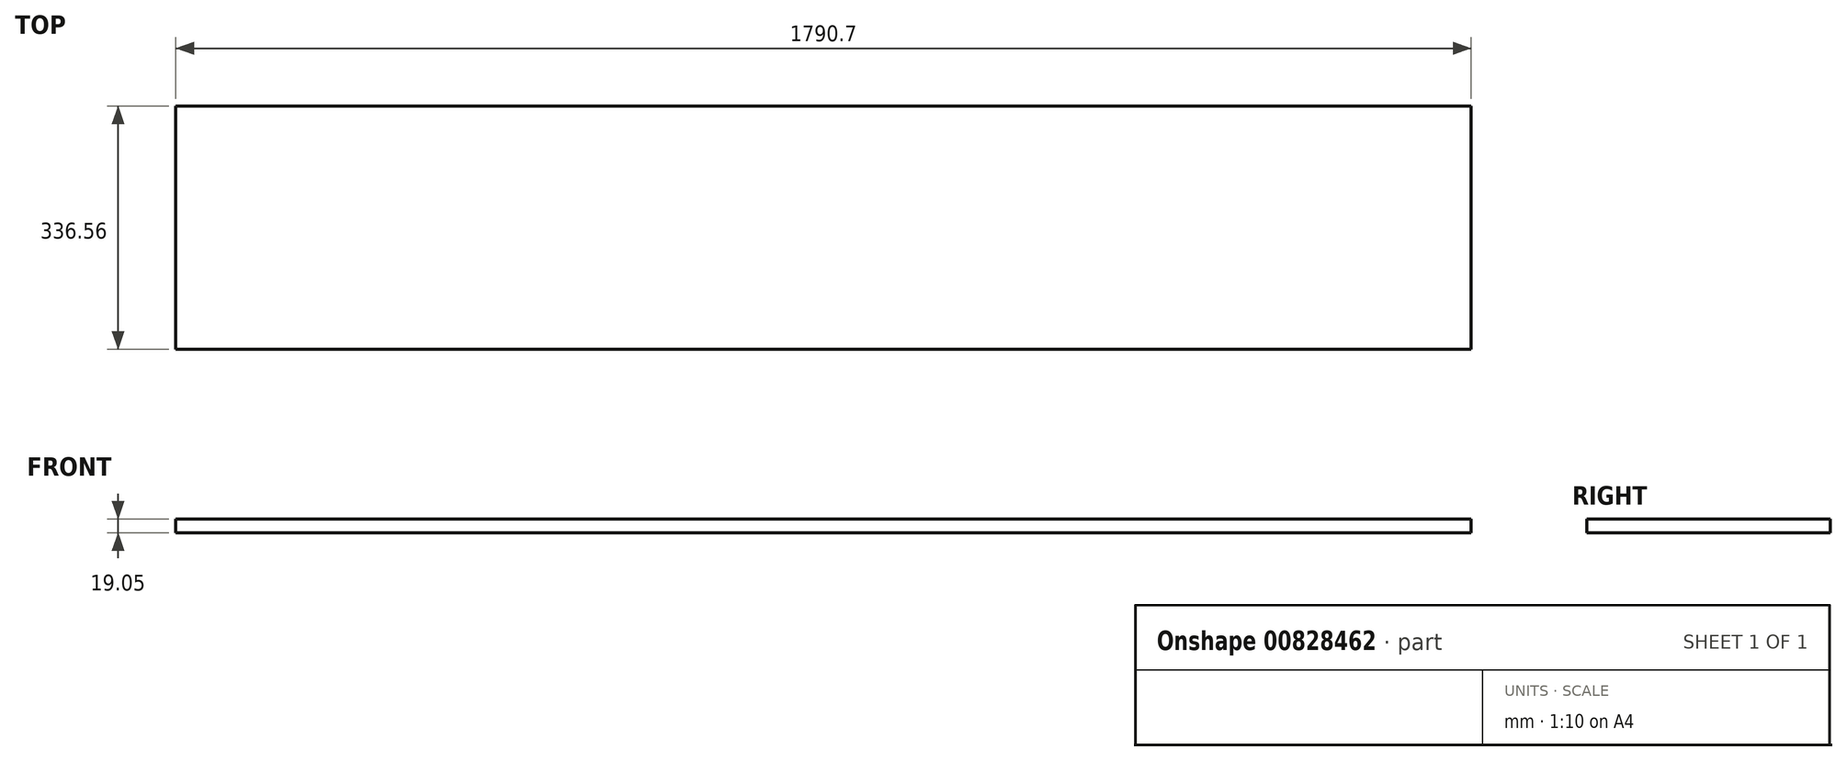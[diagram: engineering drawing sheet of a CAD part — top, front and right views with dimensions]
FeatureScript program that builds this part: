
annotation { "Feature Type Name" : "Feature", "Feature Type Description" : "" }
export const myFeature = defineFeature(function(context is Context, id is Id, definition is map)
    precondition{}
    {
        {
            var Q0;
            Q0=qCreatedBy(makeId("Top.planeOp"),FACE);
            var sketch = newSketch(context, id + "F0", { "sketchPlane" : qUnion([Q0])});
            skLineSegment(sketch, "E0.bottom", {"start": v(895.35, 168.28) * mm, "end": v(-895.35, 168.28) * mm});
            skLineSegment(sketch, "E0.top", {"start": v(895.35, -168.27) * mm, "end": v(-895.35, -168.27) * mm});
            skLineSegment(sketch, "E0.left", {"start": v(895.35, 168.28) * mm, "end": v(895.35, -168.27) * mm});
            skLineSegment(sketch, "E0.right", {"start": v(-895.35, 168.28) * mm, "end": v(-895.35, -168.27) * mm});
            skPoint(sketch, "E0.middle", {"position": v(0, 0) * mm});
            skSolve(sketch);
        }
        {
            var Q0;
            Q0=makeQuery(id+"F0.imprint","IMPRINT",FACE,{"disambiguationData":[TD([[makeQuery(id+"F0.imprint","IMPRINT",EDGE,{"derivedFrom":sQuery(id+"F0.wireOp",EDGE,"E0.bottom")}),1.0]])]});
            extrude(context, id + "F1", {"entities" : qUnion([Q0]), "depth" : 19.05 * mm, "offsetDistance" : 25.4 * mm});
        }
    });
